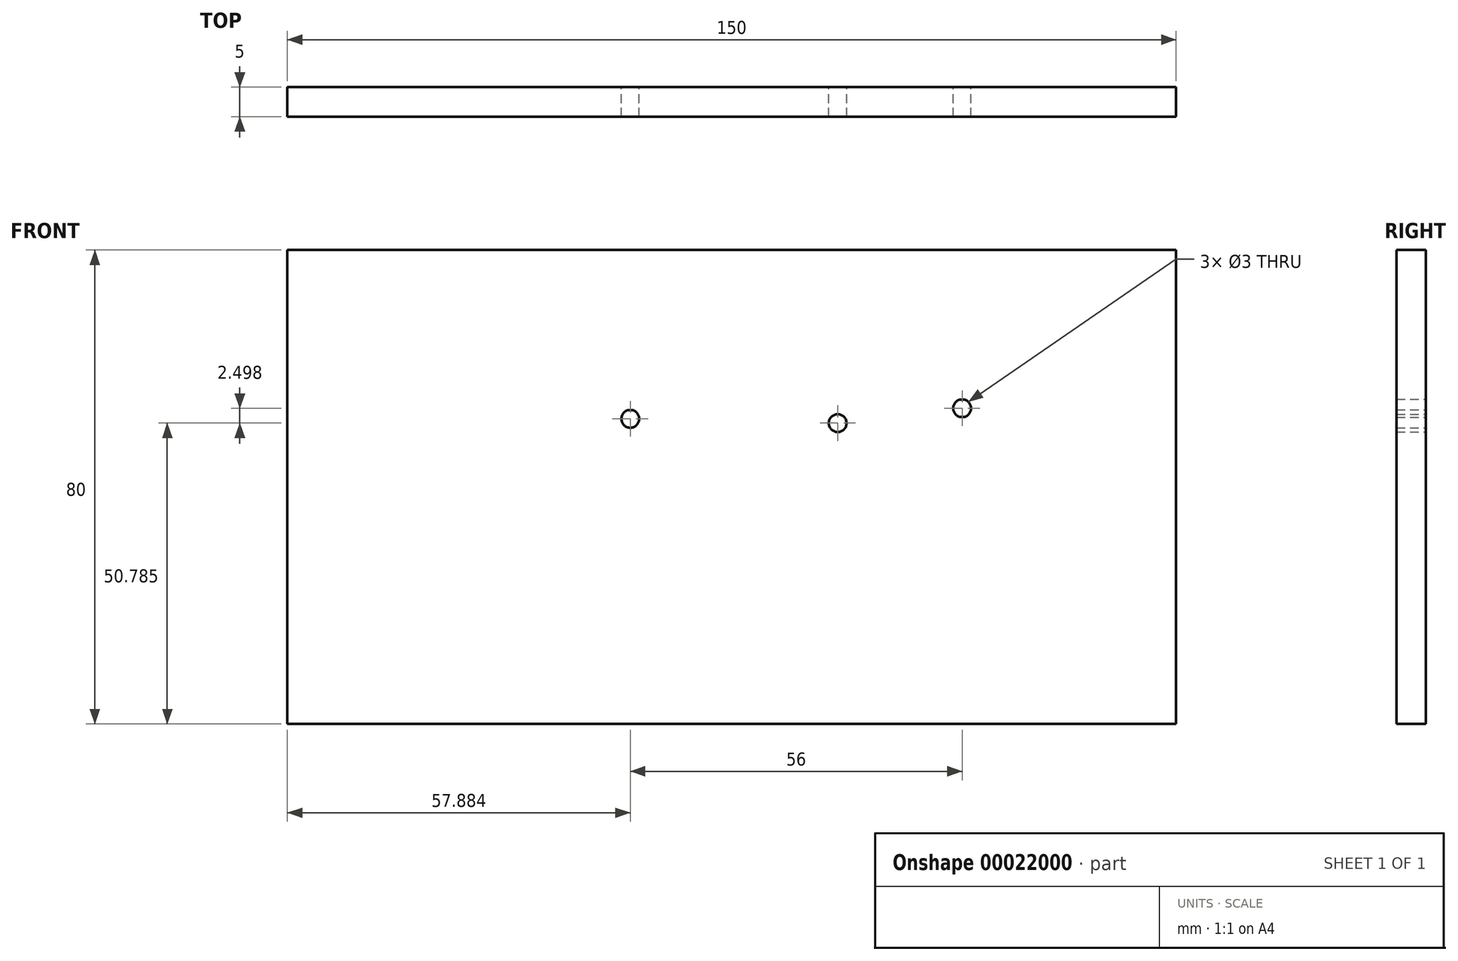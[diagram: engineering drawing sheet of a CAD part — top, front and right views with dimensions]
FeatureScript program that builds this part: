
annotation { "Feature Type Name" : "Feature", "Feature Type Description" : "" }
export const myFeature = defineFeature(function(context is Context, id is Id, definition is map)
    precondition{}
    {
        {
            var Q0;
            Q0=qCreatedBy(makeId("Front.planeOp"),FACE);
            var sketch = newSketch(context, id + "F0", { "sketchPlane" : qUnion([Q0])});
            skLineSegment(sketch, "E0.bottom", {"start": v(-77.8, 36.96) * mm, "end": v(72.2, 36.96) * mm});
            skLineSegment(sketch, "E0.top", {"start": v(-77.8, -43.04) * mm, "end": v(72.2, -43.04) * mm});
            skLineSegment(sketch, "E0.left", {"start": v(-77.8, 36.96) * mm, "end": v(-77.8, -43.04) * mm});
            skLineSegment(sketch, "E0.right", {"start": v(72.2, 36.96) * mm, "end": v(72.2, -43.04) * mm});
            skCircle(sketch, "E1", {"center": v(-19.93, 8.46) * mm, "radius": 1.5 * mm});
            skCircle(sketch, "E2", {"center": v(15.07, 7.75) * mm, "radius": 1.5 * mm});
            skCircle(sketch, "E3", {"center": v(36.07, 10.24) * mm, "radius": 1.5 * mm});
            skSolve(sketch);
        }
        {
            var Q0;
            Q0=makeQuery(id+"F0.imprint","IMPRINT",FACE,{"disambiguationData":[TD([[makeQuery(id+"F0.imprint","IMPRINT",EDGE,{"derivedFrom":sQuery(id+"F0.wireOp",EDGE,"E0.bottom")}),-1.0]])]});
            extrude(context, id + "F1", {"entities" : qUnion([Q0]), "endBound" : BoundingType.SYMMETRIC, "depth" : 5 * mm});
        }
    });
